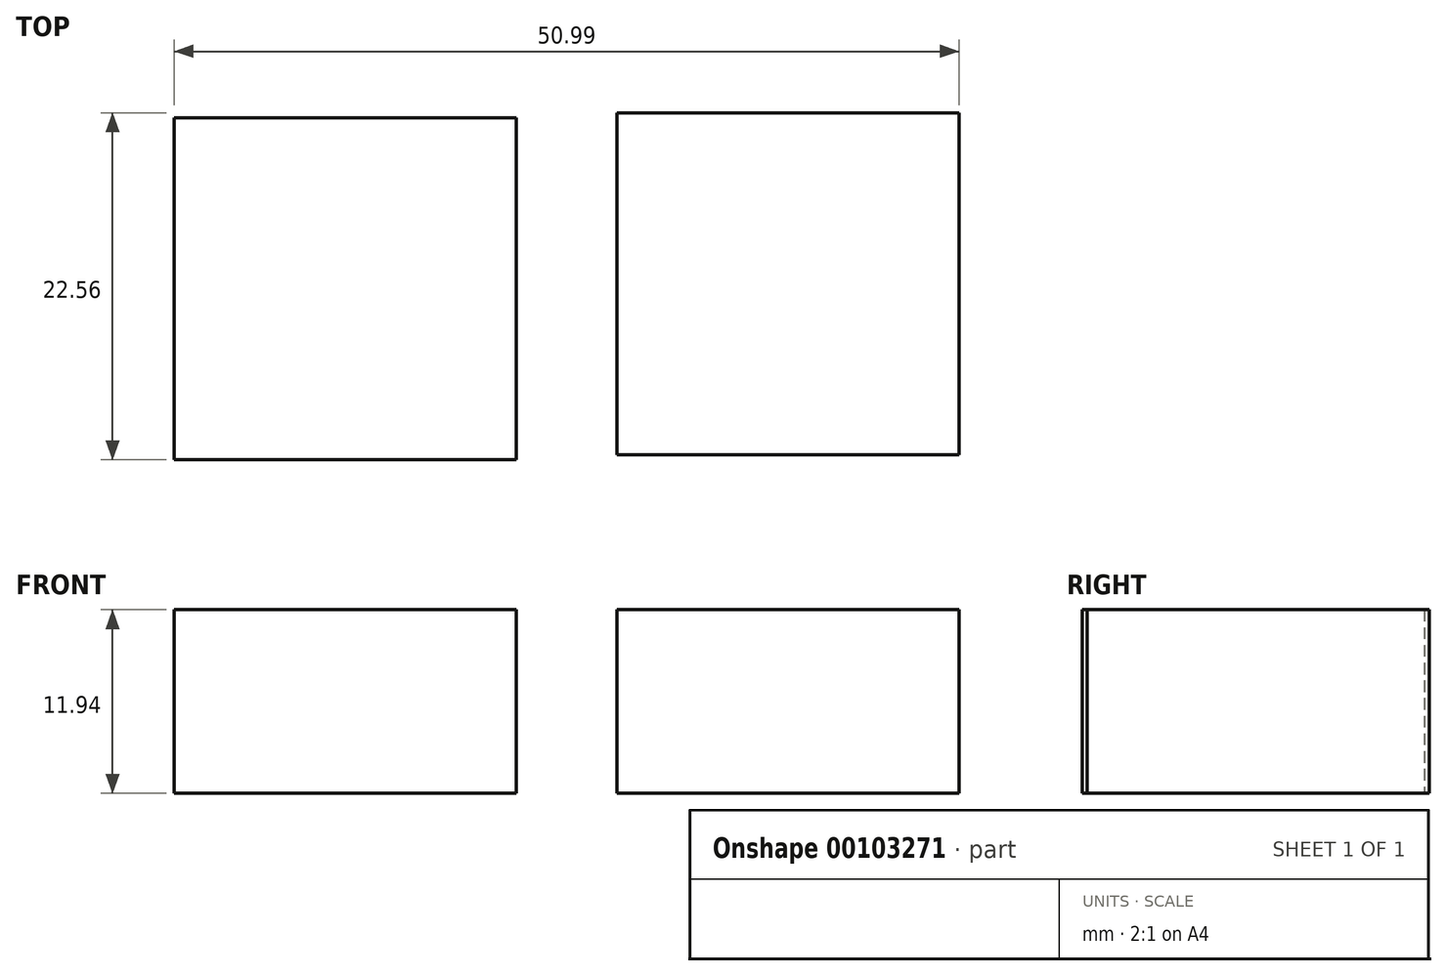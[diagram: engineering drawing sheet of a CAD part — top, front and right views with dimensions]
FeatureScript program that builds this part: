
annotation { "Feature Type Name" : "Feature", "Feature Type Description" : "" }
export const myFeature = defineFeature(function(context is Context, id is Id, definition is map)
    precondition{}
    {
        {
            var Q0;
            Q0=qCreatedBy(makeId("Top.planeOp"),FACE);
            var sketch = newSketch(context, id + "F0", { "sketchPlane" : qUnion([Q0])});
            skLineSegment(sketch, "E0.bottom", {"start": v(-29.96, 45.4) * mm, "end": v(-7.74, 45.4) * mm});
            skLineSegment(sketch, "E0.top", {"start": v(-29.96, 23.18) * mm, "end": v(-7.74, 23.18) * mm});
            skLineSegment(sketch, "E0.left", {"start": v(-29.96, 45.4) * mm, "end": v(-29.96, 23.18) * mm});
            skLineSegment(sketch, "E0.right", {"start": v(-7.74, 45.4) * mm, "end": v(-7.74, 23.18) * mm});
            skLineSegment(sketch, "E1.bottom", {"start": v(-1.2, 45.74) * mm, "end": v(21.03, 45.74) * mm});
            skLineSegment(sketch, "E1.top", {"start": v(-1.2, 23.52) * mm, "end": v(21.03, 23.52) * mm});
            skLineSegment(sketch, "E1.left", {"start": v(-1.2, 45.74) * mm, "end": v(-1.2, 23.52) * mm});
            skLineSegment(sketch, "E1.right", {"start": v(21.03, 45.74) * mm, "end": v(21.03, 23.52) * mm});
            skSolve(sketch);
        }
        {
            var Q0;
            Q0=makeQuery(id+"F0.imprint","IMPRINT",FACE,{"disambiguationData":[TD([[makeQuery(id+"F0.imprint","IMPRINT",EDGE,{"derivedFrom":sQuery(id+"F0.wireOp",EDGE,"E0.bottom")}),-1.0]])]});
            var Q1;
            Q1=makeQuery(id+"F0.imprint","IMPRINT",FACE,{"disambiguationData":[TD([[makeQuery(id+"F0.imprint","IMPRINT",EDGE,{"derivedFrom":sQuery(id+"F0.wireOp",EDGE,"E1.bottom")}),-1.0]])]});
            extrude(context, id + "F1", {"entities" : qUnion([Q0, Q1]), "depth" : 11.94 * mm});
        }
    });
